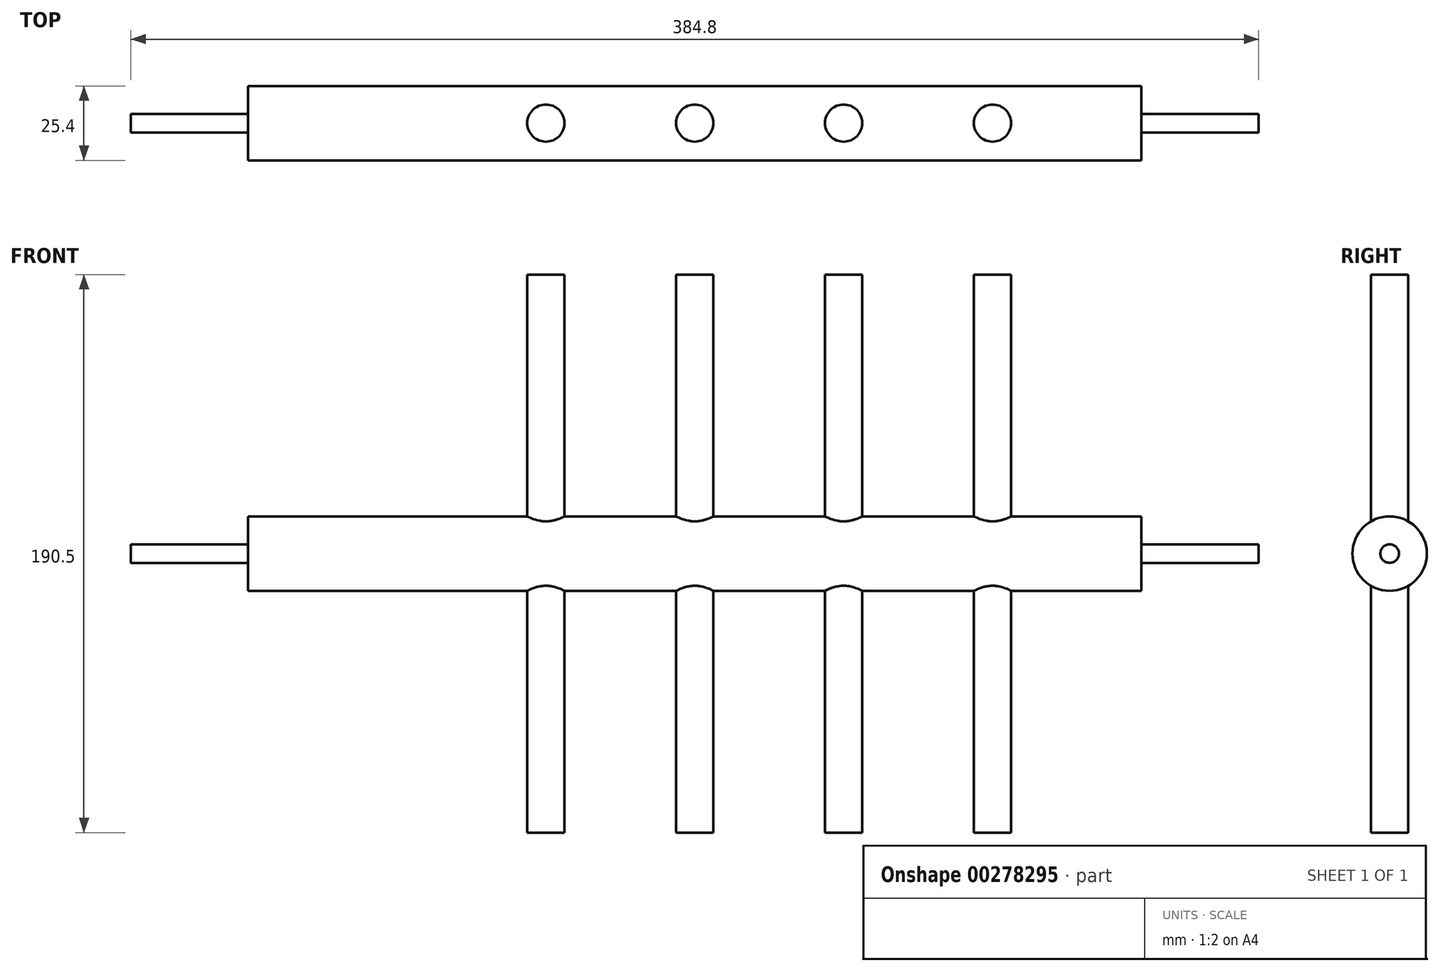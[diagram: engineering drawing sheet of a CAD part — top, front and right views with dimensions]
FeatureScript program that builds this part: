
annotation { "Feature Type Name" : "Feature", "Feature Type Description" : "" }
export const myFeature = defineFeature(function(context is Context, id is Id, definition is map)
    precondition{}
    {
        {
            var Q0;
            Q0=qCreatedBy(makeId("Right.planeOp"),FACE);
            var sketch = newSketch(context, id + "F0", { "sketchPlane" : qUnion([Q0])});
            skCircle(sketch, "E0", {"center": v(0, 0) * mm, "radius": 12.7 * mm});
            skSolve(sketch);
        }
        {
            var Q0;
            Q0=qSketchRegion(id+"F0",true);
            extrude(context, id + "F1", {"entities" : qUnion([Q0]), "depth" : 304.8 * mm});
        }
        {
            var Q0;
            Q0=makeQuery(id+"F1.opExtrude","CAP_FACE",FACE,{"disambiguationData":[OSD([sQuery(id+"F0.wireOp",EDGE,"E0")])],"isStart":false});
            var sketch = newSketch(context, id + "F2", { "sketchPlane" : qUnion([Q0])});
            skCircle(sketch, "E1", {"center": v(0, 0) * mm, "radius": 3.18 * mm});
            skSolve(sketch);
        }
        {
            var Q0;
            Q0=qSketchRegion(id+"F2",true);
            extrude(context, id + "F3", {"entities" : qUnion([Q0]), "operationType" : NewBodyOperationType.ADD, "depth" : 40 * mm});
        }
        {
            var Q0;
            Q0=makeQuery(id+"F1.opExtrude","CAP_FACE",FACE,{"disambiguationData":[OSD([sQuery(id+"F0.wireOp",EDGE,"E0")])],"isStart":true});
            var sketch = newSketch(context, id + "F4", { "sketchPlane" : qUnion([Q0])});
            skCircle(sketch, "E2", {"center": v(0, 0) * mm, "radius": 3.18 * mm});
            skSolve(sketch);
        }
        {
            var Q0;
            Q0=qSketchRegion(id+"F4",true);
            extrude(context, id + "F5", {"entities" : qUnion([Q0]), "operationType" : NewBodyOperationType.ADD, "depth" : 40 * mm});
        }
        {
            var Q0;
            Q0=qCreatedBy(makeId("Top.planeOp"),FACE);
            var sketch = newSketch(context, id + "F6", { "sketchPlane" : qUnion([Q0])});
            skCircle(sketch, "E3", {"center": v(203.2, 0) * mm, "radius": 6.35 * mm});
            skLineSegment(sketch, "E4", {"start": v(203.2, 0) * mm, "end": v(152.4, 0) * mm});
            skLineSegment(sketch, "E5", {"start": v(152.4, 0) * mm, "end": v(101.6, 0) * mm});
            skLineSegment(sketch, "E6", {"start": v(101.6, 0) * mm, "end": v(50.8, 0) * mm});
            skLineSegment(sketch, "E7", {"start": v(0, 0) * mm, "end": v(50.8, 0) * mm});
            skLineSegment(sketch, "E8", {"start": v(203.2, 0) * mm, "end": v(254, 0) * mm});
            skCircle(sketch, "E9", {"center": v(101.6, 0) * mm, "radius": 6.35 * mm});
            skCircle(sketch, "E10", {"center": v(152.4, 0) * mm, "radius": 6.35 * mm});
            skCircle(sketch, "E11", {"center": v(254, 0) * mm, "radius": 6.35 * mm});
            skSolve(sketch);
        }
        {
            var Q0;
            Q0=qSketchRegion(id+"F6",true);
            extrude(context, id + "F7", {"entities" : qUnion([Q0]), "operationType" : NewBodyOperationType.ADD, "depth" : 95.25 * mm, "hasSecondDirection" : true, "secondDirectionOppositeDirection" : true, "secondDirectionDepth" : 95.25 * mm});
        }
    });
